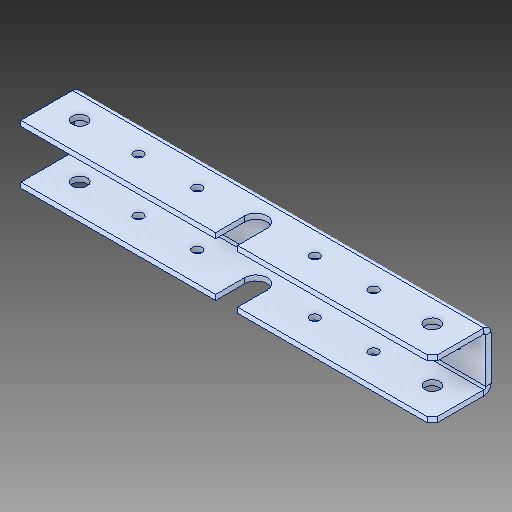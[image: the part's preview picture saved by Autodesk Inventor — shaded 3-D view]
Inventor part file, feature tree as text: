
AUTODESK INVENTOR PART (.ipt)
format: ipt  version: 2017 (Build 210142000, 142)  size: 282,112 bytes
history: native  units: in
note: dims shown in document units (in); Inventor stores cm internally (conversion verified against a paired STEP export)
features: sketch x3, hole x2, split x1, extrude x1, other x1
ambient origin geometry x8: Origin, YZ Plane, XZ Plane, XY Plane, X Axis, Y Axis, Z Axis, Center Point
bodies: Solid1 (feature_tree)
feature tree (8):
  split  "Split1"
  hole  "Hole1"  [1 undecoded]
  sketch  "Sketch3"  dims[d19=1.0in d20=0.0in d21=0.375in d22=0.75in d23=0.375in d24=0.25in d25=0.5635in d26=1.0in d27=0.8108in]
  extrude  "Extrusion2"  Depth=0.375in
  hole  "Hole3"  [1 undecoded]
  sketch  "Sketch1"  dims[d0=0.25in d1=0.25in]
  sketch  "Sketch2"  dims[d2=0.25in d3=0.75in d4=0.375in d5=0.25in d6=0.5635in d7=1.0in d8=0.8108in d9=0.375in]
  other  "Break-Corner1"
note: 2 required parameter values undecoded (feature->parameter linkage not recoverable at this tier; creation-order binding heuristic only, values carry confidence <= 0.55)
